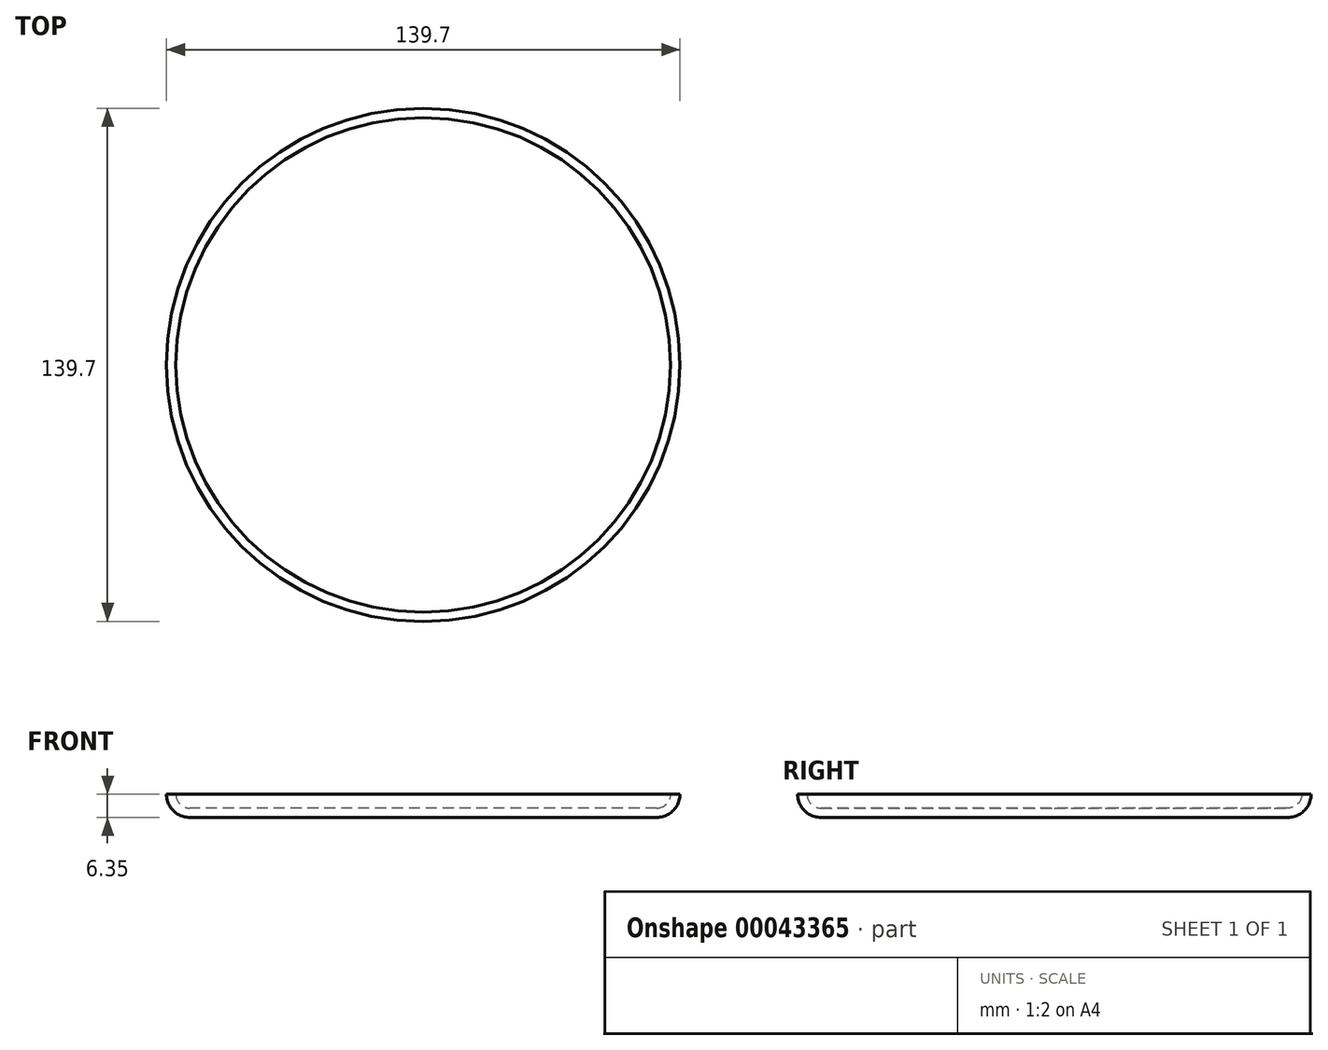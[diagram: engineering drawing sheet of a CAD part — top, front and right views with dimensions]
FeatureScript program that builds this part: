
annotation { "Feature Type Name" : "Feature", "Feature Type Description" : "" }
export const myFeature = defineFeature(function(context is Context, id is Id, definition is map)
    precondition{}
    {
        {
            var Q0;
            Q0=qCreatedBy(makeId("Top.planeOp"),FACE);
            var sketch = newSketch(context, id + "F0", { "sketchPlane" : qUnion([Q0])});
            skCircle(sketch, "E0", {"center": v(0, 0) * mm, "radius": 69.85 * mm});
            skSolve(sketch);
        }
        {
            var Q0;
            Q0 = qSketchRegion(id + "F0", true);
            extrude(context, id + "F1", {"entities" : qUnion([Q0]), "depth" : 6.35 * mm});
        }
        {
            var Q0;
            Q0=makeQuery(id+"F1.opExtrude","CAP_EDGE",EDGE,{"disambiguationData":[OSD([sQuery(id+"F0.wireOp",EDGE,"E0")])],"isStart":true});
            fillet(context, id + "F2", {"entities" : qUnion([Q0]), "radius" : 6.35 * mm, "tangentPropagation" : true, "allowEdgeOverflow" : false});
        }
        {
            var Q0;
            Q0=makeQuery(id+"F1.opExtrude","CAP_FACE",FACE,{"disambiguationData":[OSD([sQuery(id+"F0.wireOp",EDGE,"E0")])],"isStart":false});
            shell(context, id + "F3", {"entities" : qUnion([Q0]), "thickness" : 2.54 * mm});
        }
    });
